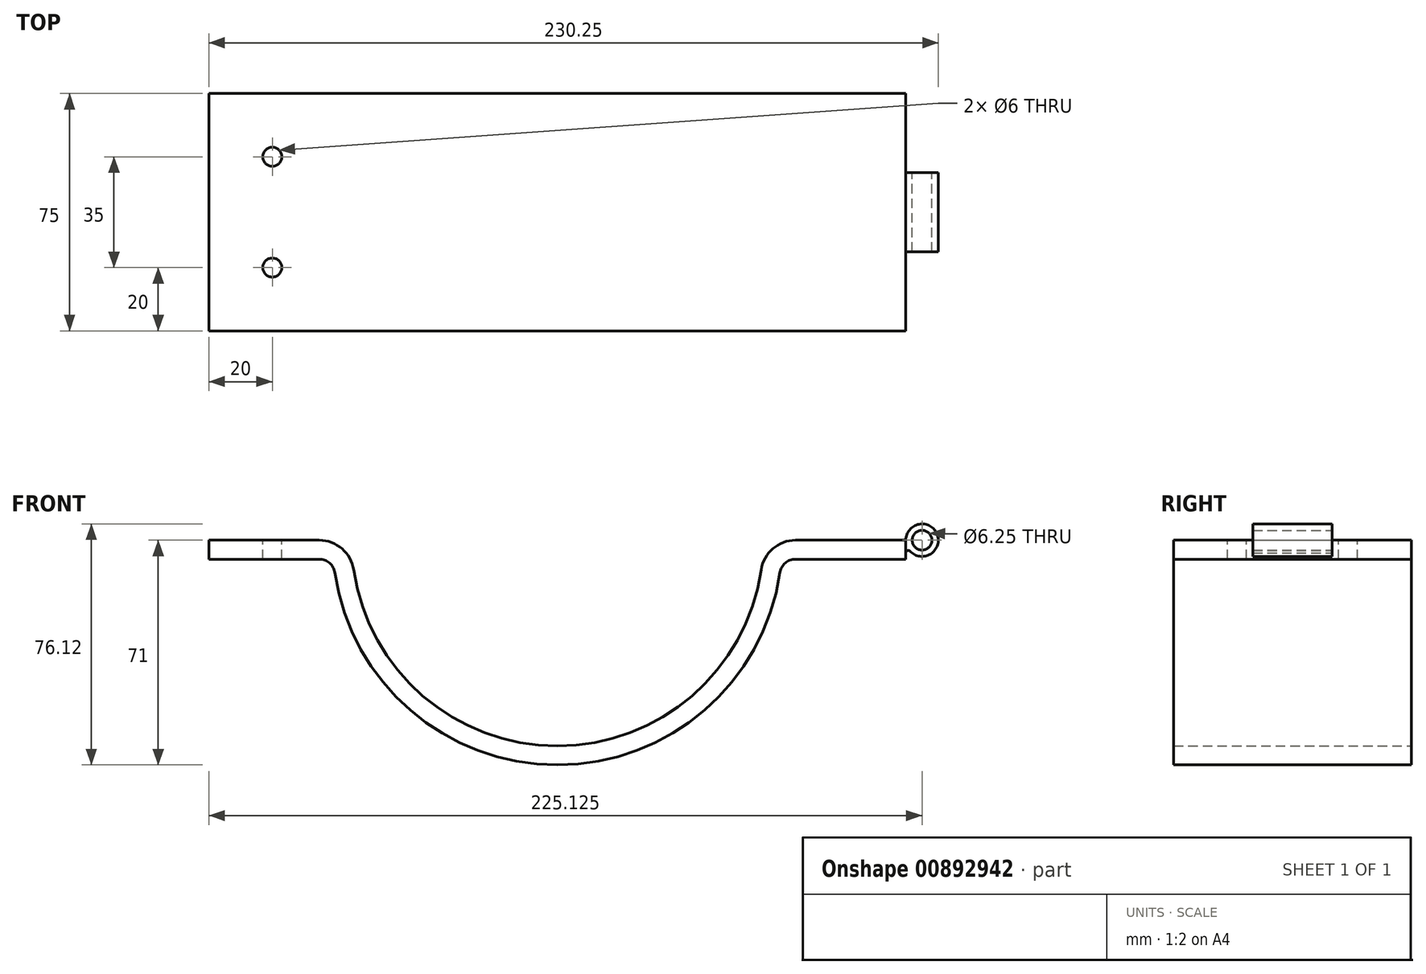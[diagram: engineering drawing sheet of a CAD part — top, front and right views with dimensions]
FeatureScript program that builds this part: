
annotation { "Feature Type Name" : "Feature", "Feature Type Description" : "" }
export const myFeature = defineFeature(function(context is Context, id is Id, definition is map)
    precondition{}
    {
        {
            var Q0;
            Q0=qCreatedBy(makeId("Front.planeOp"),FACE);
            var sketch = newSketch(context, id + "F0", { "sketchPlane" : qUnion([Q0])});
            skArc(sketch, "E0", {"start": v(-64.32, -9.4) * mm, "mid": v(0, -65) * mm, "end": v(64.32, -9.4) * mm});
            skArc(sketch, "E1", {"start": v(-70.25, -10.28) * mm, "mid": v(0, -71) * mm, "end": v(70.25, -10.28) * mm});
            skLineSegment(sketch, "E2", {"start": v(75.2, -6) * mm, "end": v(110, -6) * mm});
            skLineSegment(sketch, "E3", {"start": v(110, -6) * mm, "end": v(110, 0) * mm});
            skLineSegment(sketch, "E4.MirrorCS", {"start": v(-75.2, -6) * mm, "end": v(-110, -6) * mm});
            skLineSegment(sketch, "E5.MirrorCS", {"start": v(-110, -6) * mm, "end": v(-110, 0) * mm});
            skLineSegment(sketch, "E6", {"start": v(-110, 0) * mm, "end": v(-75.2, 0) * mm});
            skPoint(sketch, "E7.visualSharp", {"position": v(70.75, -6) * mm});
            skArc(sketch, "E7.filletArc", {"start": v(75.2, -6) * mm, "mid": v(71.93, -7.22) * mm, "end": v(70.25, -10.28) * mm});
            skPoint(sketch, "E8.newPointA", {"position": v(65, 0) * mm});
            skArc(sketch, "E8.filletArc", {"start": v(75.2, 0) * mm, "mid": v(68, -2.68) * mm, "end": v(64.32, -9.4) * mm});
            skLineSegment(sketch, "E9", {"start": v(75.2, 0) * mm, "end": v(110, 0) * mm});
            skPoint(sketch, "E10.visualSharp", {"position": v(-70.75, -6) * mm});
            skArc(sketch, "E10.filletArc", {"start": v(-70.25, -10.28) * mm, "mid": v(-71.93, -7.22) * mm, "end": v(-75.2, -6) * mm});
            skPoint(sketch, "E11.visualSharp", {"position": v(-65, 0) * mm});
            skArc(sketch, "E11.filletArc", {"start": v(-64.32, -9.4) * mm, "mid": v(-68, -2.68) * mm, "end": v(-75.2, 0) * mm});
            skSolve(sketch);
        }
        {
            var Q0;
            Q0=qSketchRegion(id+"F0",true);
            extrude(context, id + "F1", {"entities" : qUnion([Q0]), "endBound" : BoundingType.SYMMETRIC, "depth" : 75 * mm, "offsetDistance" : 25 * mm});
        }
        {
            var Q0;
            Q0=makeQuery(id+"F1.opExtrude","SWEPT_FACE",FACE,{"disambiguationData":[OSD([sQuery(id+"F0.wireOp",EDGE,"E6")])]});
            var sketch = newSketch(context, id + "F2", { "sketchPlane" : qUnion([Q0])});
            skLineSegment(sketch, "E12", {"start": v(-90, 40.03) * mm, "end": v(-90, -36.7) * mm, "construction": true});
            skLineSegment(sketch, "E13", {"start": v(-136.24, 0) * mm, "end": v(178.68, 0) * mm, "construction": true});
            skPoint(sketch, "E13.endSnap0", {"position": v(-75.2, 0) * mm});
            skLineSegment(sketch, "E14", {"start": v(0, -92.93) * mm, "end": v(0, 90.35) * mm, "construction": true});
            skCircle(sketch, "E15", {"center": v(-90, 17.5) * mm, "radius": 3 * mm});
            skCircle(sketch, "E16.MirrorC", {"center": v(-90, -17.5) * mm, "radius": 3 * mm});
            skSolve(sketch);
        }
        {
            var Q0;
            Q0=qCreatedBy(makeId("Front.planeOp"),FACE);
            var sketch = newSketch(context, id + "F3", { "sketchPlane" : qUnion([Q0])});
            skArc(sketch, "E17", {"start": v(111.34, -3.45) * mm, "mid": v(119.9, 1.85) * mm, "end": v(110, 0) * mm});
            skCircle(sketch, "E18", {"center": v(115.12, 0) * mm, "radius": 3.12 * mm});
            skArc(sketch, "E19", {"start": v(111.34, -3.45) * mm, "mid": v(110.5, -3.25) * mm, "end": v(110, -3.97) * mm});
            skLineSegment(sketch, "E20", {"start": v(110, -3.97) * mm, "end": v(110, 0) * mm});
            skSolve(sketch);
        }
        {
            var Q0;
            Q0=qSketchRegion(id+"F3",true);
            var Q1;
            Q1=makeQuery(id+"F1.opExtrude","CAP_FACE",FACE,{"disambiguationData":[OSD([sQuery(id+"F0.wireOp",EDGE,"E0"),sQuery(id+"F0.wireOp",EDGE,"E1"),sQuery(id+"F0.wireOp",EDGE,"E2"),sQuery(id+"F0.wireOp",EDGE,"E3"),sQuery(id+"F0.wireOp",EDGE,"E4.MirrorCS"),sQuery(id+"F0.wireOp",EDGE,"E5.MirrorCS"),sQuery(id+"F0.wireOp",EDGE,"E6"),sQuery(id+"F0.wireOp",EDGE,"E7.filletArc"),sQuery(id+"F0.wireOp",EDGE,"E8.filletArc"),sQuery(id+"F0.wireOp",EDGE,"E9"),sQuery(id+"F0.wireOp",EDGE,"E10.filletArc"),sQuery(id+"F0.wireOp",EDGE,"E11.filletArc")])],"isStart":false});
            var Q2;
            Q2=makeQuery(id+"F1.opExtrude","CAP_FACE",FACE,{"disambiguationData":[OSD([sQuery(id+"F0.wireOp",EDGE,"E0"),sQuery(id+"F0.wireOp",EDGE,"E1"),sQuery(id+"F0.wireOp",EDGE,"E2"),sQuery(id+"F0.wireOp",EDGE,"E3"),sQuery(id+"F0.wireOp",EDGE,"E4.MirrorCS"),sQuery(id+"F0.wireOp",EDGE,"E5.MirrorCS"),sQuery(id+"F0.wireOp",EDGE,"E6"),sQuery(id+"F0.wireOp",EDGE,"E7.filletArc"),sQuery(id+"F0.wireOp",EDGE,"E8.filletArc"),sQuery(id+"F0.wireOp",EDGE,"E9"),sQuery(id+"F0.wireOp",EDGE,"E10.filletArc"),sQuery(id+"F0.wireOp",EDGE,"E11.filletArc")])],"isStart":true});
            extrude(context, id + "F4", {"entities" : qUnion([Q0]), "endBound" : BoundingType.UP_TO_SURFACE, "depth" : 25 * mm, "endBoundEntityFace" : qUnion([Q1]), "offsetDistance" : 25 * mm, "hasSecondDirection" : true, "secondDirectionBound" : SecondDirectionBoundingType.UP_TO_SURFACE, "secondDirectionOppositeDirection" : true, "secondDirectionDepth" : 25 * mm, "secondDirectionBoundEntityFace" : qUnion([Q2])});
        }
        {
            var Q0;
            Q0=qCreatedBy(makeId("Top.planeOp"),FACE);
            var sketch = newSketch(context, id + "F5", { "sketchPlane" : qUnion([Q0])});
            skLineSegment(sketch, "E21.bottom", {"start": v(110, -12.5) * mm, "end": v(125.71, -12.5) * mm});
            skLineSegment(sketch, "E21.top", {"start": v(110, -39.4) * mm, "end": v(125.71, -39.4) * mm});
            skLineSegment(sketch, "E21.left", {"start": v(110, -12.5) * mm, "end": v(110, -39.4) * mm});
            skLineSegment(sketch, "E21.right", {"start": v(125.71, -12.5) * mm, "end": v(125.71, -39.4) * mm});
            skLineSegment(sketch, "E22.bottom", {"start": v(110, 12.5) * mm, "end": v(132.58, 12.5) * mm});
            skLineSegment(sketch, "E22.top", {"start": v(110, 40.03) * mm, "end": v(132.58, 40.03) * mm});
            skLineSegment(sketch, "E22.left", {"start": v(110, 12.5) * mm, "end": v(110, 40.03) * mm});
            skLineSegment(sketch, "E22.right", {"start": v(132.58, 12.5) * mm, "end": v(132.58, 40.03) * mm});
            skSolve(sketch);
        }
        {
            var Q0;
            Q0=qSketchRegion(id+"F5",true);
            extrude(context, id + "F6", {"entities" : qUnion([Q0]), "operationType" : NewBodyOperationType.REMOVE, "endBound" : BoundingType.THROUGH_ALL, "oppositeDirection" : true, "depth" : 25 * mm, "offsetDistance" : 25 * mm, "hasSecondDirection" : true, "secondDirectionBound" : SecondDirectionBoundingType.THROUGH_ALL, "secondDirectionOppositeDirection" : false, "secondDirectionDepth" : 25 * mm});
        }
        {
            var Q0;
            Q0 = qSketchRegion(id + "F2", true);
            extrude(context, id + "F7", {"entities" : qUnion([Q0]), "operationType" : NewBodyOperationType.REMOVE, "endBound" : BoundingType.THROUGH_ALL, "oppositeDirection" : true, "depth" : 25 * mm, "offsetDistance" : 25 * mm});
        }
    });
